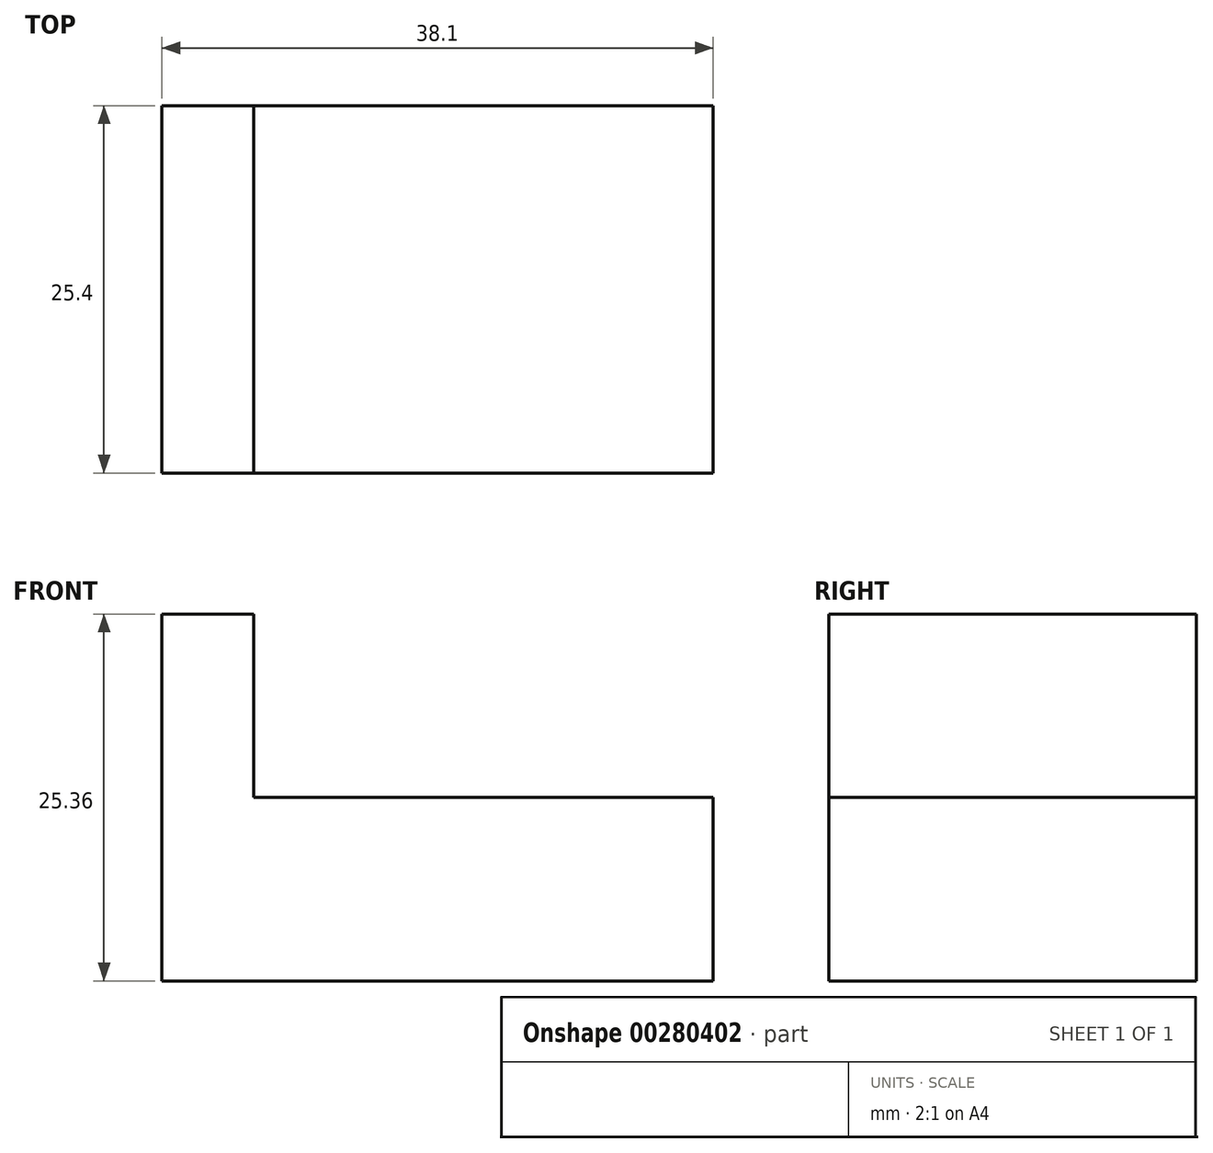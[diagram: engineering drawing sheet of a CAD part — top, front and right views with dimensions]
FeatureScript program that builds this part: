
annotation { "Feature Type Name" : "Feature", "Feature Type Description" : "" }
export const myFeature = defineFeature(function(context is Context, id is Id, definition is map)
    precondition{}
    {
        {
            var Q0;
            Q0=qCreatedBy(makeId("Front.planeOp"),FACE);
            var sketch = newSketch(context, id + "F0", { "sketchPlane" : qUnion([Q0])});
            skLineSegment(sketch, "E0", {"start": v(0, 0) * mm, "end": v(0, 25.36) * mm});
            skLineSegment(sketch, "E1", {"start": v(0, 25.36) * mm, "end": v(6.35, 25.36) * mm});
            skLineSegment(sketch, "E2", {"start": v(6.35, 25.36) * mm, "end": v(6.35, 12.7) * mm});
            skLineSegment(sketch, "E3", {"start": v(6.35, 12.7) * mm, "end": v(38.1, 12.7) * mm});
            skLineSegment(sketch, "E4", {"start": v(38.1, 12.7) * mm, "end": v(38.1, 0) * mm});
            skLineSegment(sketch, "E5", {"start": v(38.1, 0) * mm, "end": v(0, 0) * mm});
            skSolve(sketch);
        }
        {
            var Q0;
            Q0 = qSketchRegion(id + "F0", true);
            extrude(context, id + "F1", {"entities" : qUnion([Q0]), "depth" : 25.4 * mm});
        }
    });
